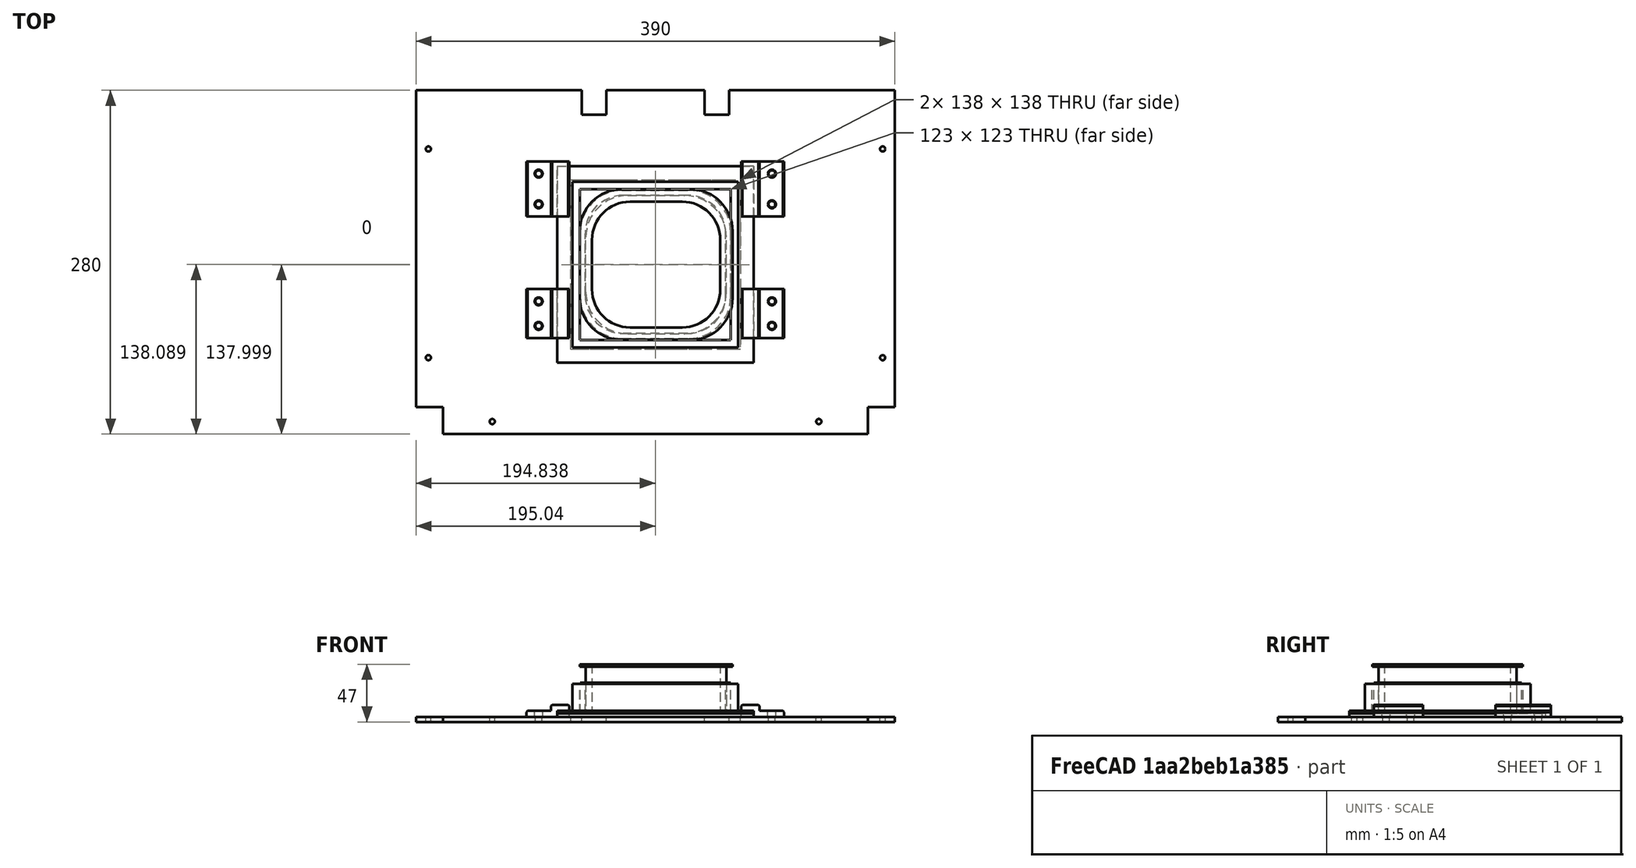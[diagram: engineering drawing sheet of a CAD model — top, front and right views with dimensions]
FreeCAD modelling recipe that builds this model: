
FCSTD DOCUMENT  (FreeCAD 0.14R3703 (Git))
Label: premontaje_cubeta
License: CC-BY 3.0
LicenseURL: http://creativecommons.org/licenses/by/3.0/
objects: Part::Cylinder×14, Part::Cut×14, Part::Feature×11
note: 39 computed .brp shape members not serialized (recipe doc carries the construction recipe); baked Part::Feature solids carry a one-line shape summary decoded from their .brp

FEATURE [Part::Feature] Pad  label="portacubeta"
  shape: bbox 390 x 280 x 4 mm, 22 faces (baked)
FEATURE [Part::Feature] Pad001  label="cubeta_cristal"
  Placement = pos=(-0.2016,-9.1113,7) rot=(0,0,1;0rad)
  shape: bbox 160 x 160 x 24 mm, 15 faces (baked)
FEATURE [Part::Feature] Box  label="cristal_cubeta"
  Placement = pos=(-80.2016,-89.1113,4) rot=(0,0,1;0rad)
  shape: bbox 160 x 160 x 3 mm, 6 faces (baked)
FEATURE [Part::Feature] Cut  label="guia_cubeta_ant_izq"
  Placement = pos=(104.798,-69.1113,4) rot=(0,0,1;1.5708rad)
  shape: bbox 35 x 40 x 10 mm, 15 faces (baked)
FEATURE [Part::Feature] Cut001  label="guia_cubeta_frontal_der"
  Placement = pos=(-105.202,-29.1113,4) rot=(0,0,-1;1.5708rad)
  shape: bbox 35 x 40 x 10 mm, 15 faces (baked)
FEATURE [Part::Feature] Fusion  label="guia_cubeta_pos_izq001"
  Placement = pos=(-105.202,74.8887,4) rot=(0,0,-1;1.5708rad)
  shape: bbox 35 x 45 x 10 mm, 16 faces (baked)
FEATURE [Part::Feature] Fusion001  label="guia_cubeta_pos_der001"
  Placement = pos=(104.798,29.8887,4) rot=(0,0,1;1.5708rad)
  shape: bbox 35 x 45 x 10 mm, 16 faces (baked)
FEATURE [Part::Feature] Fusion002  label="cube_flex001"
  Placement = pos=(57.7319,-65.4407,47) rot=(0,1,0;3.14159rad)
  shape: bbox 124.5 x 122.5 x 40 mm, 27 faces (baked)
FEATURE [Part::Feature] Fillet  label="aro_cube_flex"
  Placement = pos=(-61.3016,-69.2901,7) rot=(0,0,1;0rad)
  shape: bbox 122.5 x 120.5 x 25 mm, 18 faces (baked)
FEATURE [Part::Cylinder] Cylinder  label="Cilindro"
  Angle = 360
  Height = 23
  Placement = pos=(-95.2016,64.8887,-14) rot=(0,0,1;0rad)
  Radius = 2.7
FEATURE [Part::Cylinder] Cylinder001  label="Cilindro001"
  Angle = 360
  Height = 23
  Placement = pos=(94.7984,-39.1113,-14) rot=(0,0,1;0rad)
  Radius = 2.7
FEATURE [Part::Cylinder] Cylinder002  label="Cilindro002"
  Angle = 360
  Height = 23
  Placement = pos=(94.7984,-59.1113,-14) rot=(0,0,1;0rad)
  Radius = 2.7
FEATURE [Part::Cylinder] Cylinder003  label="Cilindro003"
  Angle = 360
  Height = 23
  Placement = pos=(94.7984,39.8887,-14) rot=(0,0,1;0rad)
  Radius = 2.7
FEATURE [Part::Cylinder] Cylinder004  label="Cilindro004"
  Angle = 360
  Height = 23
  Placement = pos=(94.7984,64.8887,-14) rot=(0,0,1;0rad)
  Radius = 2.7
FEATURE [Part::Cylinder] Cylinder005  label="Cilindro005"
  Angle = 360
  Height = 23
  Placement = pos=(-95.202,-59.1113,-14) rot=(0,0,1;0rad)
  Radius = 2.7
FEATURE [Part::Cylinder] Cylinder006  label="Cilindro006"
  Angle = 360
  Height = 23
  Placement = pos=(-95.2016,39.8887,-14) rot=(0,0,1;0rad)
  Radius = 2.7
FEATURE [Part::Cylinder] Cylinder007  label="Cilindro007"
  Angle = 360
  Height = 23
  Placement = pos=(-95.202,-39.1113,-14) rot=(0,0,1;0rad)
  Radius = 2.7
FEATURE [Part::Cut] Cut002
  Base = -> Pad
  Tool = -> Cylinder
FEATURE [Part::Cut] Cut003
  Base = -> Cut002
  Tool = -> Cylinder001
FEATURE [Part::Cut] Cut004
  Base = -> Cut003
  Tool = -> Cylinder002
FEATURE [Part::Cut] Cut005
  Base = -> Cut004
  Tool = -> Cylinder003
FEATURE [Part::Cut] Cut006
  Base = -> Cut005
  Tool = -> Cylinder007
FEATURE [Part::Cut] Cut007
  Base = -> Cut006
  Tool = -> Cylinder006
FEATURE [Part::Cut] Cut008
  Base = -> Cut007
  Tool = -> Cylinder005
FEATURE [Part::Cut] Cut009  label="base_cubeta_tornillos"
  Base = -> Cut008
  Tool = -> Cylinder004
FEATURE [Part::Feature] Cut010  label="base_cubeta_tornillos_cubeta"
  shape: bbox 390 x 280 x 4 mm, 30 faces (baked)
FEATURE [Part::Cylinder] Cylinder008  label="Cilindro008"
  Angle = 360
  Height = 25
  Placement = pos=(-185,-85,-8) rot=(0,0,1;0rad)
  Radius = 2.1
FEATURE [Part::Cylinder] Cylinder009  label="Cilindro009"
  Angle = 360
  Height = 25
  Placement = pos=(-185,85,-8) rot=(0,0,1;0rad)
  Radius = 2.1
FEATURE [Part::Cylinder] Cylinder010  label="Cilindro010"
  Angle = 360
  Height = 25
  Placement = pos=(185,85,-8) rot=(0,0,1;0rad)
  Radius = 2.1
FEATURE [Part::Cylinder] Cylinder011  label="Cilindro011"
  Angle = 360
  Height = 25
  Placement = pos=(185,-85,-8) rot=(0,0,1;0rad)
  Radius = 2.1
FEATURE [Part::Cylinder] Cylinder012  label="Cilindro012"
  Angle = 360
  Height = 25
  Placement = pos=(-133,-137,-8) rot=(0,0,1;0rad)
  Radius = 2.1
FEATURE [Part::Cylinder] Cylinder013  label="Cilindro013"
  Angle = 360
  Height = 25
  Placement = pos=(133,-137,-8) rot=(0,0,1;0rad)
  Radius = 2.1
FEATURE [Part::Cut] Cut011
  Base = -> Cut010
  Tool = -> Cylinder008
FEATURE [Part::Cut] Cut012
  Base = -> Cut011
  Tool = -> Cylinder013
FEATURE [Part::Cut] Cut013
  Base = -> Cut012
  Tool = -> Cylinder012
FEATURE [Part::Cut] Cut014
  Base = -> Cut013
  Tool = -> Cylinder011
FEATURE [Part::Cut] Cut015
  Base = -> Cut014
  Tool = -> Cylinder010
FEATURE [Part::Cut] Cut016
  Base = -> Cut015
  Tool = -> Cylinder009
FEATURE [Part::Feature] Cut017  label="base_cubeta_tornillos_estructura"
  shape: bbox 390 x 280 x 4 mm, 36 faces (baked)
